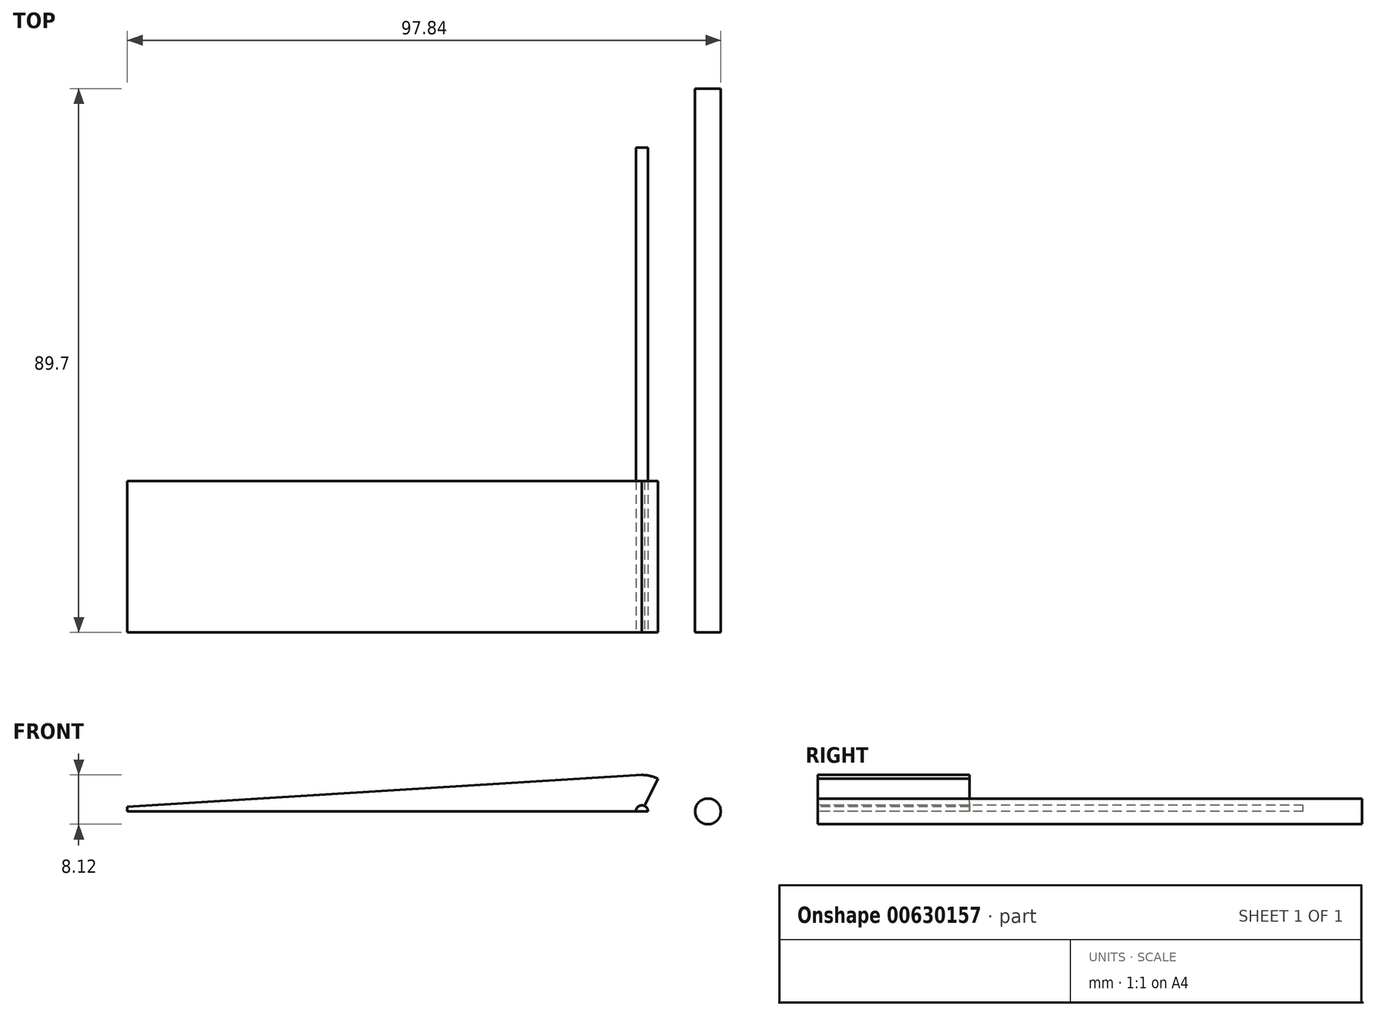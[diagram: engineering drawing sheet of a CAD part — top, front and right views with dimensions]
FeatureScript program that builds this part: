
annotation { "Feature Type Name" : "Feature", "Feature Type Description" : "" }
export const myFeature = defineFeature(function(context is Context, id is Id, definition is map)
    precondition{}
    {
        {
            var Q0;
            Q0=qCreatedBy(makeId("Front.planeOp"),FACE);
            var sketch = newSketch(context, id + "F0", { "sketchPlane" : qUnion([Q0])});
            skArc(sketch, "E0", {"start": v(2.65, 5.38) * mm, "mid": v(1, 5.92) * mm, "end": v(-0.74, 5.95) * mm});
            skLineSegment(sketch, "E1", {"start": v(0, 6) * mm, "end": v(-84.84, 0.74) * mm});
            skLineSegment(sketch, "E2", {"start": v(1, 0) * mm, "end": v(-84.84, 0) * mm});
            skLineSegment(sketch, "E3", {"start": v(-84.84, 0) * mm, "end": v(-84.84, 0.74) * mm});
            skLineSegment(sketch, "E4", {"start": v(-84.84, 0) * mm, "end": v(1, 0) * mm, "construction": true});
            skPoint(sketch, "E5.MirrorCS.end.orphan", {"position": v(-84.84, -0.74) * mm});
            skPoint(sketch, "E5.MirrorCS.start.orphan", {"position": v(-84.84, 0) * mm});
            skCircle(sketch, "E6", {"center": v(0, 0) * mm, "radius": 1 * mm});
            skLineSegment(sketch, "E7", {"start": v(0, 0) * mm, "end": v(2.65, 5.38) * mm});
            skLineSegment(sketch, "E8.trimOffspring", {"start": v(6, 0) * mm, "end": v(22.06, 0) * mm, "construction": true});
            skPoint(sketch, "E9.orphan", {"position": v(-96.33, 0) * mm});
            skSolve(sketch);
        }
        {
            var Q0;
            {var subQ0=sQuery(id+"F0.wireOp",EDGE,"E2");Q0=makeQuery(id+"F0.imprint","IMPRINT",FACE,{"disambiguationData":[TD([[makeQuery(id+"F0.imprint","IMPRINT",EDGE,{"derivedFrom":subQ0}),-1.0]])]});}
            extrude(context, id + "F1", {"entities" : qUnion([Q0]), "oppositeDirection" : true, "depth" : 80 * mm, "offsetDistance" : 25 * mm});
        }
        {
            var Q0;
            Q0=qCreatedBy(makeId("Front.planeOp"),FACE);
            var sketch = newSketch(context, id + "F2", { "sketchPlane" : qUnion([Q0])});
            skCircle(sketch, "E10", {"center": v(10.88, 0) * mm, "radius": 2.12 * mm});
            skSolve(sketch);
        }
        {
            var Q0;
            Q0 = qSketchRegion(id + "F2", true);
            extrude(context, id + "F3", {"entities" : qUnion([Q0]), "operationType" : NewBodyOperationType.ADD, "oppositeDirection" : true, "depth" : 89.7 * mm, "offsetDistance" : 25 * mm});
        }
        {
            var Q0;
            {var subQ0=sQuery(id+"F0.wireOp",EDGE,"E3");Q0=makeQuery(id+"F0.imprint","IMPRINT",FACE,{"disambiguationData":[TD([[makeQuery(id+"F0.imprint","IMPRINT",EDGE,{"derivedFrom":subQ0}),-1.0]])]});}
            extrude(context, id + "F4", {"entities" : qUnion([Q0]), "oppositeDirection" : true, "depth" : 25 * mm, "offsetDistance" : 25 * mm});
        }
    });
